# Revit family: _Camera-Security-Panasonic-Long_distance_IR_illumination-PTZ-Dome-Network-S6532LNSSeries_2019ver
name_source: partatom
category: Security Devices
units: mm (PartAtom-declared; Revit-internal decimal feet)

## family parameters
Cut with Voids When Loaded = No
Host = Face
Maintain Annotation Orientation = No
OmniClass Number = 23.85.10.14.11
OmniClass Title = Cameras
Part Type = Normal
Room Calculation Point = No
Round Connector Dimension = Use Diameter
Shared = No

## types (4) — shared parameters
Alarm Input Or Output Specification = ALARM IN 1 (DAY/NIGHT IN, Auto time adjustment) (x1), ALARM IN 2 (ALARM OUT) (x1), ALARM IN 3 (AUX OUT) (x1)
Angle Of View = 66
Audio In = Yes
Audio Out = Yes
Base Height = 9.52756 "
Communication Ports = 10Base-T / 100Base-TX, RJ45 connector
Day Or Night = Yes
Diameter = 9.80315 "
Equipment Abbreviation = SC
Family Version = 1.0.0
HFOV Max 169 = 66.00°
HFOV Max 43 = 51.00°
Has POE = Yes
Height = 18.30709 "
IP Or Analog = IP
IR Panel Meterial = Panasonic - Target
Indoor Or Outdoor = Outdoor
Lens Axis Offset = 1.37795 "
Lens Material = Laminate, Navy
Manufacturer = Panasonic
Minimum Illumination = 0.015 lx
Model Disclaimer = Contact Panasonic for more information
Mounting Positions = Mount Dependent
Operational Humidity = 10 to 100 % (no condensation)
Pan Max = 360.00°
Pan Min = 0.00°
Panning Range = 360
Pendant Height = 1.9685 "
Power Active = 55.0 W
Product Documentation Link = https://bizpartner.panasonic.net
Product Material = Paint - Panasonic - Silver
Product Page URL = https://security.panasonic.com
Provide Feedback = https://www.surveymonkey.com
Regulatory Compliance = UL (UL60950-1), c-UL (CSA C22.2 No.60950-1), CE, IEC60950-1, FCC (Part15 ClassA), ICES003 ClassA, EN55032 ClassA, EN55024
Shock resistance = Yes
Tilt Max = 210.00°
Tilt Min = -30.00°
Tilting Range = -30 to +210
URL = http://security.panasonic.com
VFOV Max 169 = 39.00°
VFOV Max 43 = 39.00°
Vandal Resistant = Yes
Voltage AC = 24 V
Water and Dust Resistance = Yes
Weight = 18.10 lb
Wide Dynamic Range = Yes
z Camera Head Origin Height = 6.02362 "
z Const Pan Handle Length = 27.55906 "
z Const Tilt Base Length = 14.17323 "
z Const Tilt Base2 Length = 19.68504 "
z Const Tilt Handle Length = 14.17323 "
z Const Yaw Base Length = 9.84252 "
z Const Yaw Base2 Length = 500.00°
z Const Yaw Handle Length = 9.25197 "
z VV Viewpoint Depth Max = 1.62598 "
z VV Viewpoint Depth Min = 1.62598 "
zero-valued in all types: Default Elevation, z Camera Resolution Type

## per-type parameters (varying)
| type | Date Last Modified | Description | HFOV Min 169 | HFOV Min 43 | Operational Temperature | Part Description | Storage Temperature | VFOV Min 169 | VFOV Min 43 |
| WV-S6532LN | 2019/06/11 | Security Camera, Super Dynamic Full HD, Long Distance IR Illumination, Weather Proof, PTZ, Dome, Network, WV-S6532LN | 3.40° | 2.60° | –40 °C to +60 °C {–40 °F to +140 °F} | Security Camera, Super Dynamic Full HD, Long Distance IR Illumination, Weather Proof, PTZ, Dome, Network, WV-S6532LN | –40 °C to +60 °C {–40 °F to +140 °F} | 2.00° | 2.00° |
| WV-X6533LN | 2019/06/11 | Security Camera, Super Dynamic Full HD, Long Distance IR Illumination, Weather Proof, PTZ, Dome, Network, WV-X6533LN | 1.90° | 1.40° | –50 °C to +60 °C {–58 °F to +140 °F} | Security Camera, Super Dynamic Full HD, Long Distance IR Illumination, Weather Proof, PTZ, Dome, Network, WV-X6533LN | –50 °C to +60 °C {–58 °F to +140 °F} | 1.10° | 1.10° |
| WV-X6533LNS | 2020/10/28 | Security Camera, Super Dynamic Full HD, Long Distance IR Illumination, Weather Proof, PTZ, Dome, Network, WV-X6533LNS | 1.90° | 1.40° | –50 °C to +60 °C {–58 °F to +140 °F} | Security Camera, Super Dynamic Full HD, Long Distance IR Illumination, Weather Proof, PTZ, Dome, Network, WV-X6533LNS | –50 °C to +60 °C {–58 °F to +140 °F} | 1.10° | 1.10° |
| WV-S6532LNS | 2020/10/28 | Security Camera, Super Dynamic Full HD, Long Distance IR Illumination, Weather Proof, PTZ, Dome, Network, WV-S6532LNS | 3.40° | 2.60° | –40 °C to +60 °C {–40 °F to +140 °F} | Security Camera, Super Dynamic Full HD, Long Distance IR Illumination, Weather Proof, PTZ, Dome, Network, WV-S6532LNS | –40 °C to +60 °C {–40 °F to +140 °F} | 2.00° | 2.00° |

note: column(s) folded — value = type name in every type: Model, Part Number

## geometry (parser evidence)
native form markers: Blend x2, Sweep x17
no freeform markers — native parametric forms only
